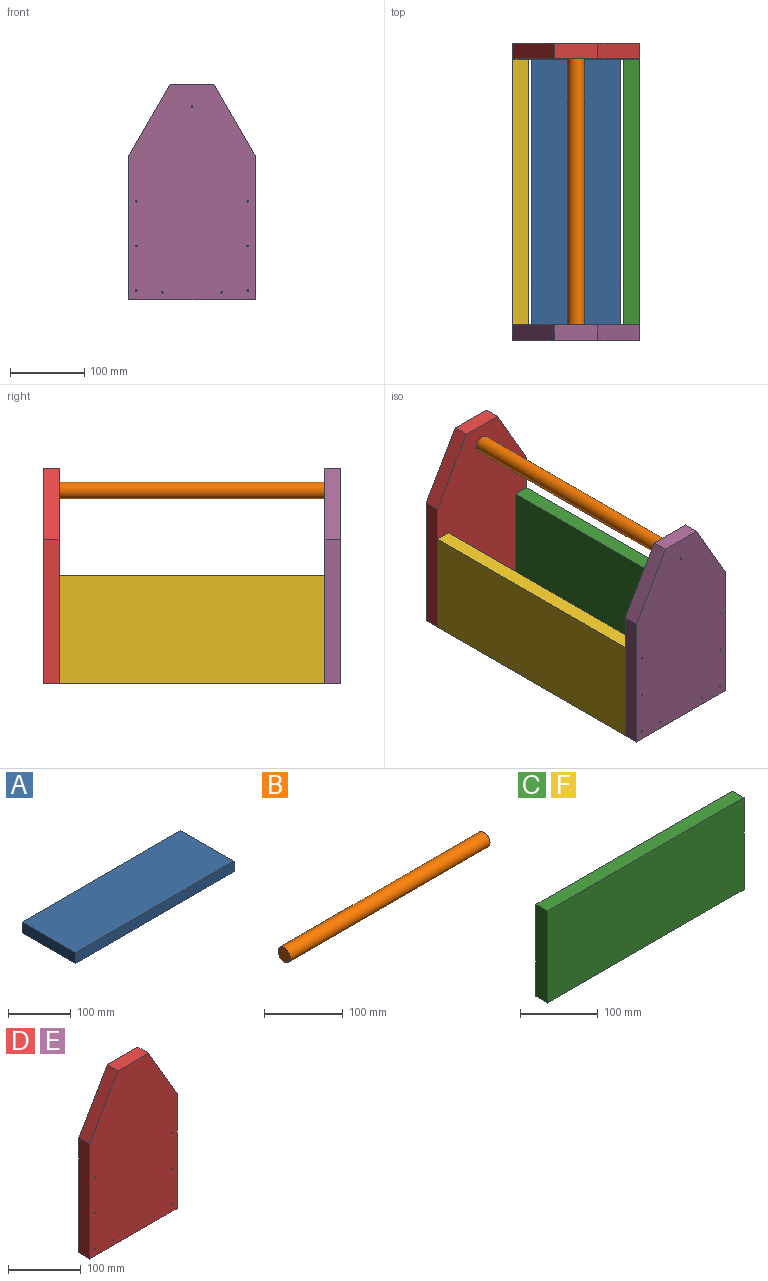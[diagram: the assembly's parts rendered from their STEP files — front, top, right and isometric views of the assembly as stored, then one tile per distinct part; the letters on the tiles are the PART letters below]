
ASSEMBLY  parts=6 mates=5
PART A: 6 faces, bbox 358x120x21 mm
  f0: plane 120x21mm, normal (-1,0,0), area 2520mm2, adj f1,f3,f4,f5
  f1: plane 358x21mm, normal (0,-1,0), area 7518mm2, adj f0,f2,f4,f5
  f2: plane 120x21mm, normal (1,0,0), area 2520mm2, adj f1,f3,f4,f5
  f3: plane 358x21mm, normal (0,1,0), area 7518mm2, adj f0,f2,f4,f5
  f4: plane 358x120mm, normal (0,0,1), area 42960mm2, adj f0,f1,f2,f3
  f5: plane 358x120mm, normal (0,0,-1), area 42960mm2, adj f0,f1,f2,f3
PART B: 3 faces, bbox 358x22x22 mm
  f0: cylinder r=11mm len=358mm, axis (-1,0,0), area 24743.2mm2, adj f1,f2
  f1: plane 22x22mm, normal (1,0,0), area 380.1mm2, adj f0
  f2: plane 22x22mm, normal (-1,0,0), area 380.1mm2, adj f0
PART C: 6 faces, bbox 358x21x145 mm
  f0: plane 145x21mm, normal (-1,0,0), area 3045mm2, adj f1,f3,f4,f5
  f1: plane 358x21mm, normal (0,0,-1), area 7518mm2, adj f0,f2,f4,f5
  f2: plane 145x21mm, normal (1,0,0), area 3045mm2, adj f1,f3,f4,f5
  f3: plane 358x21mm, normal (0,0,1), area 7518mm2, adj f0,f2,f4,f5
  f4: plane 358x145mm, normal (0,-1,0), area 51910mm2, adj f0,f1,f2,f3
  f5: plane 358x145mm, normal (0,1,0), area 51910mm2, adj f0,f1,f2,f3
PART D: 17 faces, bbox 170x21x290 mm
  f0: plane 194x21mm, normal (-1,0,0), area 4074mm2, adj f1,f5,f6,f7
  f1: plane 170x21mm, normal (0,0,-1), area 3570mm2, adj f0,f2,f6,f7
  f2: plane 194x21mm, normal (1,0,0), area 4074mm2, adj f1,f3,f6,f7
  f3: plane 96x55.43mm, normal (0.87,0,0.5), area 2327.9mm2, adj f2,f4,f6,f7
  f4: plane 59.15x21mm, normal (0,0,1), area 1242.1mm2, adj f3,f5,f6,f7
  f5: plane 96x55.43mm, normal (-0.87,0,0.5), area 2327.9mm2, adj f0,f4,f6,f7
  f6: plane 290x170mm, normal (0,-1,0), area 43950.9mm2, adj f0,f1,f2,f3,f4,f5,f8,f9
  f7: plane 290x170mm, normal (0,1,0), area 43950.9mm2, adj f0,f1,f2,f3,f4,f5,f8,f9
  f8: cylinder r=1mm len=21mm, axis (0,-1,0), area 131.9mm2, adj f6,f7
  f9: cylinder r=1mm len=21mm, axis (0,-1,0), area 131.9mm2, adj f6,f7
  f10: cylinder r=1mm len=21mm, axis (0,-1,0), area 131.9mm2, adj f6,f7
  f11: cylinder r=1mm len=21mm, axis (0,-1,0), area 131.9mm2, adj f6,f7
  f12: cylinder r=1mm len=21mm, axis (0,-1,0), area 131.9mm2, adj f6,f7
  f13: cylinder r=1mm len=21mm, axis (0,-1,0), area 131.9mm2, adj f6,f7
  f14: cylinder r=1mm len=21mm, axis (0,-1,0), area 131.9mm2, adj f6,f7
  f15: cylinder r=1mm len=21mm, axis (0,-1,0), area 131.9mm2, adj f6,f7
  f16: cylinder r=1mm len=21mm, axis (0,-1,0), area 131.9mm2, adj f6,f7
PART E: same geometry as D
PART F: same geometry as C
PLACE A rot(axis=(0,0,1),90deg) t=(166.18,54.22,5.91)mm
PLACE B rot(axis=(0.58,-0.58,-0.58),120deg) t=(106.18,412.22,265.91)mm
PLACE C rot(axis=(0,0,-1),90deg) t=(191.18,412.22,5.91)mm
PLACE D rot(axis=(0,0,1),180deg) t=(191.18,412.22,5.91)mm
PLACE E rot(axis=(0.26,0.94,-0.22),0deg) t=(21.18,54.22,5.91)mm
PLACE F rot(axis=(0,0,1),90deg) t=(21.18,54.22,5.91)mm
MATE fastened C.f2 <-> E.f7  axis (0,-1,0) through (191.18,54.22,5.91)mm
MATE fastened F.f0 <-> E.f7  axis (0,-1,0) through (21.18,54.22,5.91)mm
MATE fastened A.f0 <-> E.f7  axis (0,-1,0) through (106.18,54.22,5.91)mm
MATE fastened B.f0 <-> E.f14  axis (0,-1,0) through (106.18,54.22,265.91)mm
MATE fastened D.f7 <-> A.f2  axis (0,-1,0) through (106.18,412.22,5.91)mm
